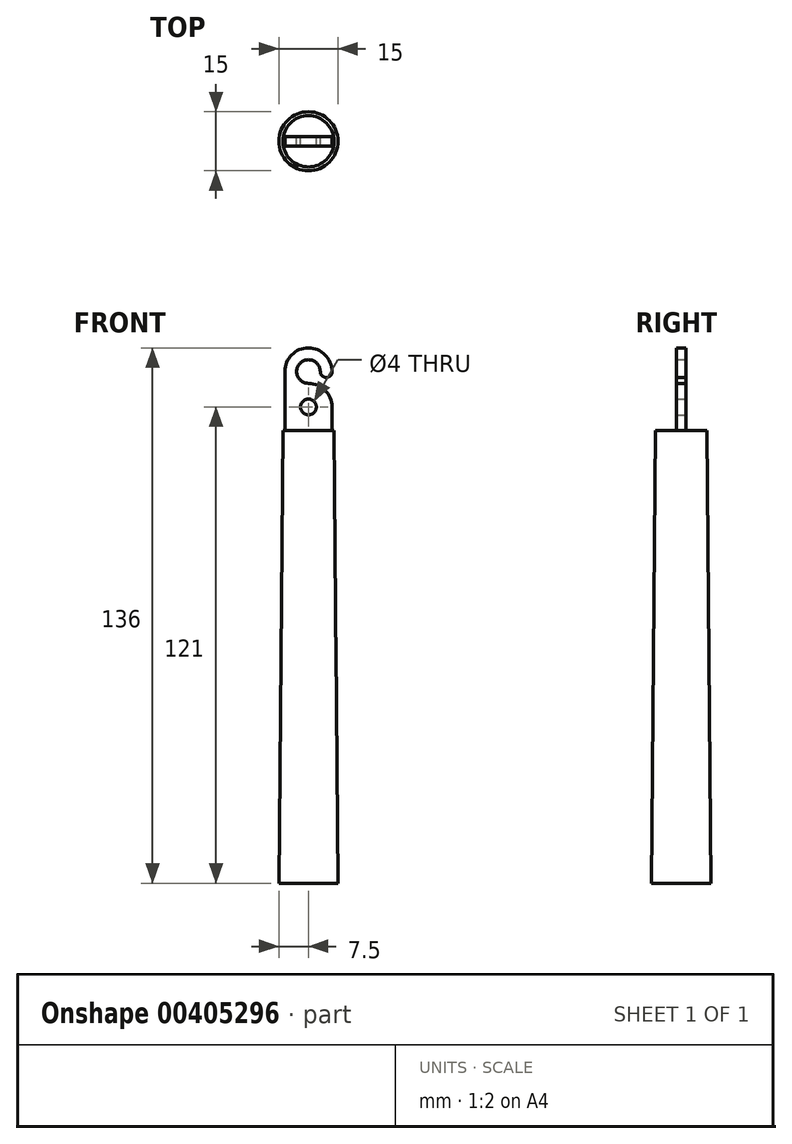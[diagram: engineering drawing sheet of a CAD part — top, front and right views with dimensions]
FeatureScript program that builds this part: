
annotation { "Feature Type Name" : "Feature", "Feature Type Description" : "" }
export const myFeature = defineFeature(function(context is Context, id is Id, definition is map)
    precondition{}
    {
        {
            var Q0;
            Q0=qCreatedBy(makeId("Front.planeOp"),FACE);
            var sketch = newSketch(context, id + "F0", { "sketchPlane" : qUnion([Q0])});
            skLineSegment(sketch, "E0.top", {"start": v(-6, 0) * mm, "end": v(6, 0) * mm});
            skLineSegment(sketch, "E0.left", {"start": v(-6, 15) * mm, "end": v(-6, 0) * mm});
            skArc(sketch, "E1", {"start": v(6, 15) * mm, "mid": v(0, 21) * mm, "end": v(-6, 15) * mm});
            skArc(sketch, "E2", {"start": v(3, 15) * mm, "mid": v(-2.12, 17.12) * mm, "end": v(0, 12) * mm});
            skCircle(sketch, "E3", {"center": v(0, 6) * mm, "radius": 2 * mm});
            skArc(sketch, "E4", {"start": v(6, 6) * mm, "mid": v(4.24, 10.24) * mm, "end": v(0, 12) * mm});
            skLineSegment(sketch, "E5", {"start": v(6, 0) * mm, "end": v(6, 6) * mm});
            skArc(sketch, "E6", {"start": v(3, 15) * mm, "mid": v(4.5, 13.5) * mm, "end": v(6, 15) * mm});
            skPoint(sketch, "E7.start.orphan", {"position": v(3, 15) * mm});
            skSolve(sketch);
        }
        {
            var Q0;
            Q0=makeQuery(id+"F0.imprint","IMPRINT",FACE,{"disambiguationData":[TD([[makeQuery(id+"F0.imprint","IMPRINT",EDGE,{"derivedFrom":sQuery(id+"F0.wireOp",EDGE,"E0.top")}),1.0]])]});
            extrude(context, id + "F1", {"entities" : qUnion([Q0]), "endBound" : BoundingType.SYMMETRIC, "depth" : 2.5 * mm});
        }
        {
            var Q0;
            Q0=qCreatedBy(makeId("Right.planeOp"),FACE);
            var sketch = newSketch(context, id + "F2", { "sketchPlane" : qUnion([Q0])});
            skLineSegment(sketch, "E8", {"start": v(0, 0) * mm, "end": v(0, -115) * mm});
            skLineSegment(sketch, "E9", {"start": v(0, 0) * mm, "end": v(-6.5, 0) * mm});
            skLineSegment(sketch, "E10", {"start": v(-6.5, 0) * mm, "end": v(-7.5, -115) * mm});
            skLineSegment(sketch, "E11", {"start": v(-7.5, -115) * mm, "end": v(0, -115) * mm});
            skSolve(sketch);
        }
        {
            var Q0;
            Q0=makeQuery(id+"F2.imprint","IMPRINT",FACE,{"disambiguationData":[TD([[makeQuery(id+"F2.imprint","IMPRINT",EDGE,{"derivedFrom":sQuery(id+"F2.wireOp",EDGE,"E8")}),-1.0]])]});
            var Q1;
            Q1=sQuery(id+"F2.wireOp",EDGE,"E8");
            revolve(context, id + "F3", {"operationType" : NewBodyOperationType.ADD, "entities" : qUnion([Q0]), "axis" : qUnion([Q1]), "revolveType" : RevolveType.FULL});
        }
    });
